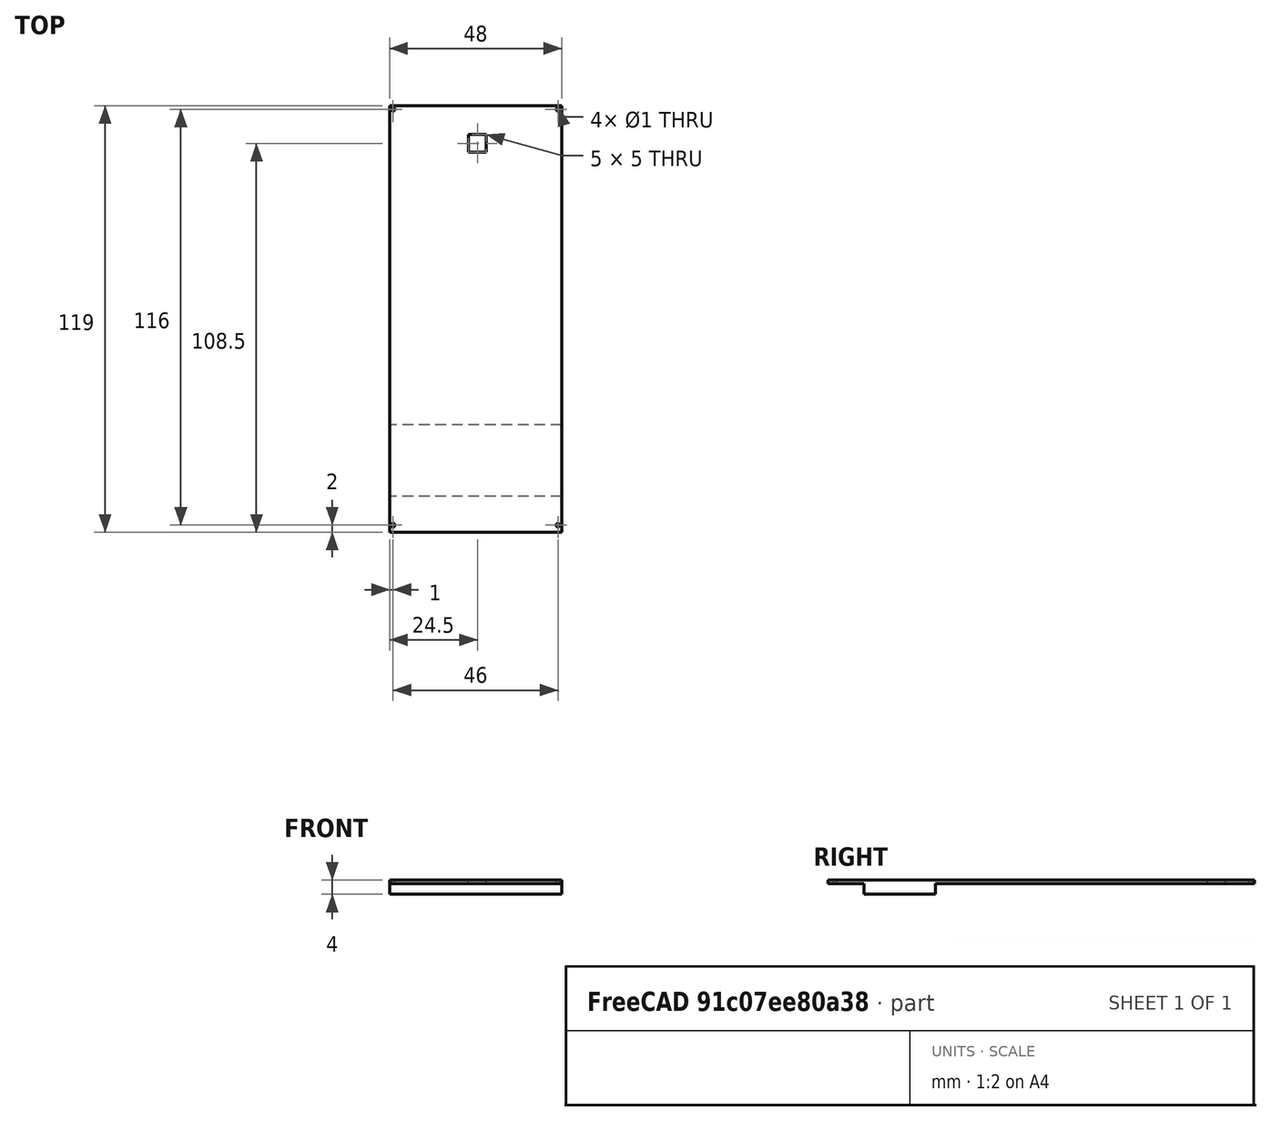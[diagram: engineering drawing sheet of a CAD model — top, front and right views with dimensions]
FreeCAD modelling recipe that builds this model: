
FCSTD DOCUMENT  (FreeCAD 0.18.4R)
Label: lid
License: All rights reserved
LicenseURL: http://en.wikipedia.org/wiki/All_rights_reserved
objects: Part::FeaturePython×6, Part::Box×5, Part::Cylinder×4
note: 15 computed .brp shape members not serialized (recipe doc carries the construction recipe); baked Part::Feature solids carry a one-line shape summary decoded from their .brp

FEATURE [Part::Box] Box023  label="Cube021"
  AttacherType = Attacher::AttachEngine3D
  Height = 1
  Length = 89
  Placement = pos=(44,30,34) rot=(0,0,1;1.5708rad)
  Width = 48
FEATURE [Part::Box] Box021  label="Cube019"
  AttacherType = Attacher::AttachEngine3D
  Height = 1
  Length = 20
  Placement = pos=(44,10,34) rot=(0,0,1;1.5708rad)
  Width = 48
FEATURE [Part::Box] Box022  label="Cube020"
  AttacherType = Attacher::AttachEngine3D
  Height = 3
  Length = 20
  Placement = pos=(44,10,31) rot=(0,0,1;1.5708rad)
  Width = 48
FEATURE [Part::Box] Box020  label="Cube018"
  AttacherType = Attacher::AttachEngine3D
  Height = 1
  Length = 10
  Placement = pos=(44,-9.8e-15,34) rot=(0,0,1;1.5708rad)
  Width = 48
FEATURE [Part::Cylinder] Cylinder007
  Angle = 360
  AttacherType = Attacher::AttachEngine3D
  Height = 10
  Placement = pos=(-3,118,29) rot=(0,0,1;0rad)
  Radius = 0.5
FEATURE [Part::Cylinder] Cylinder006
  Angle = 360
  AttacherType = Attacher::AttachEngine3D
  Height = 10
  Placement = pos=(43,118,29) rot=(0,0,1;0rad)
  Radius = 0.5
FEATURE [Part::Cylinder] Cylinder004
  Angle = 360
  AttacherType = Attacher::AttachEngine3D
  Height = 10
  Placement = pos=(-3,2,29) rot=(0,0,1;0rad)
  Radius = 0.5
FEATURE [Part::Cylinder] Cylinder005
  Angle = 360
  AttacherType = Attacher::AttachEngine3D
  Height = 10
  Placement = pos=(43,2,29) rot=(0,0,1;0rad)
  Radius = 0.5
FEATURE [Part::Box] Box024  label="Cube022"
  AttacherType = Attacher::AttachEngine3D
  Height = 1
  Length = 5
  Placement = pos=(18,106,75) rot=(0,0,1;0rad)
  Width = 5
FEATURE [Part::FeaturePython] Connect001  # WARN: FeaturePython — macro-defined, semantics opaque (R4)
  Objects = -> [Box020,Box022,Box021,Box023]
  Placement = pos=(0,0,-1) rot=(0,0,1;0rad)
  Tolerance = 0
FEATURE [Part::FeaturePython] Cutout010  # WARN: FeaturePython — macro-defined, semantics opaque (R4)
  Base = -> Connect001
  Tolerance = 0
  Tool = -> Cylinder006
FEATURE [Part::FeaturePython] Cutout011  # WARN: FeaturePython — macro-defined, semantics opaque (R4)
  Base = -> Cutout010
  Tolerance = 0
  Tool = -> Cylinder005
FEATURE [Part::FeaturePython] Cutout012  # WARN: FeaturePython — macro-defined, semantics opaque (R4)
  Base = -> Cutout011
  Tolerance = 0
  Tool = -> Cylinder004
FEATURE [Part::FeaturePython] Cutout013  # WARN: FeaturePython — macro-defined, semantics opaque (R4)
  Base = -> Cutout012
  Placement = pos=(0,0,42) rot=(0,0,1;0rad)
  Tolerance = 0
  Tool = -> Cylinder007
FEATURE [Part::FeaturePython] Cutout014  label="lid"  # WARN: FeaturePython — macro-defined, semantics opaque (R4)
  Base = -> Cutout013
  Tolerance = 0
  Tool = -> Box024
